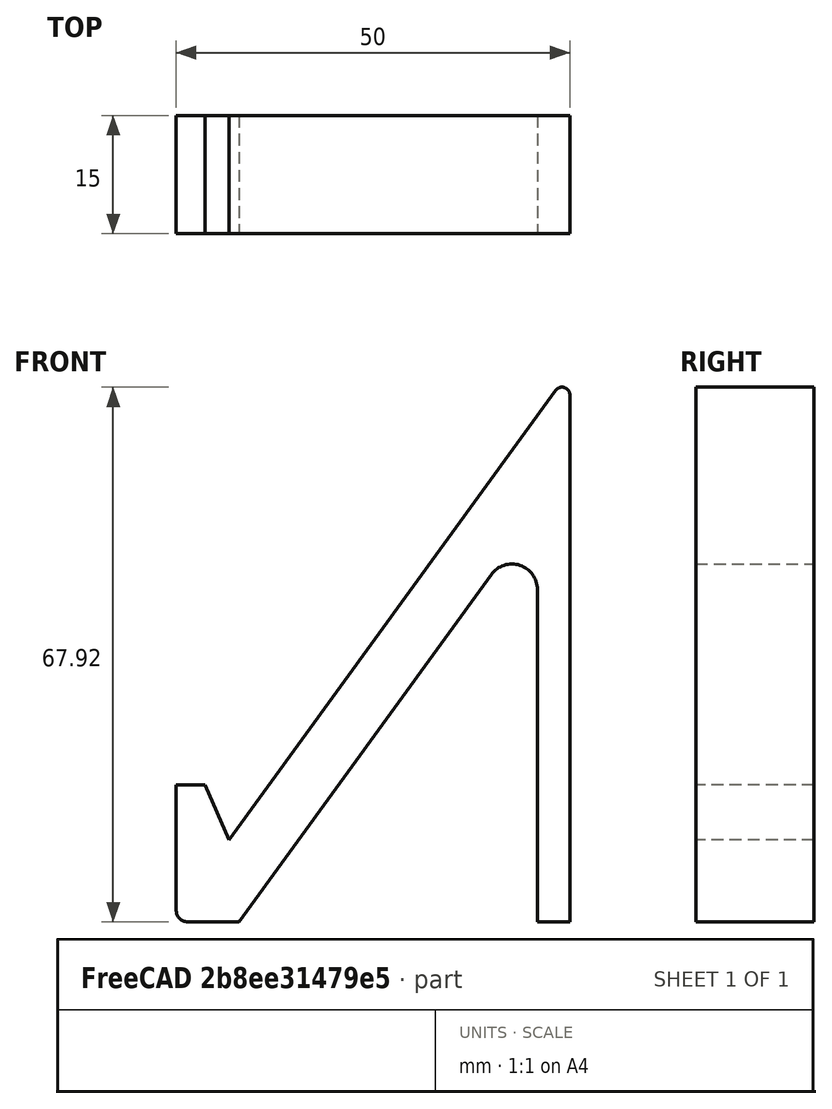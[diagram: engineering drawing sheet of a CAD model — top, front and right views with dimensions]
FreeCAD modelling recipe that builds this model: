
FCSTD DOCUMENT  (FreeCAD 1.1R20260414 (Git shallow))
Label: swordStand
License: All rights reserved
LicenseURL: https://en.wikipedia.org/wiki/All_rights_reserved
objects: App::Point×1, Sketcher::SketchObject×1, PartDesign::Pad×1, PartDesign::Fillet×1, PartDesign::Body×1
note: 9 computed .brp shape members not serialized (recipe doc carries the construction recipe); baked Part::Feature solids carry a one-line shape summary decoded from their .brp

FEATURE [App::Point] Origin001
  Role = Origin
FEATURE [Sketcher::SketchObject] Sketch
  ArcFitTolerance = 1e-06
  AttachmentSupport = -> [Origin]
  ExternalTypes = [0]
  FullyConstrained = false
  MakeInternals = false
  MapMode = 5
  Placement = pos=(0,0,0) rot=(1,0,0;1.5708rad)
  _ExternalGeoVersion = 1
  sketch-geometry (17):
    g0: LineSegment [constr] StartX=0 StartY=0 StartZ=0 EndX=50 EndY=0 EndZ=0
    g1: LineSegment [constr] StartX=50 StartY=0 StartZ=0 EndX=50 EndY=70 EndZ=0
    g2: LineSegment [constr] StartX=50 StartY=70 StartZ=0 EndX=0 EndY=70 EndZ=0
    g3: LineSegment [constr] StartX=0 StartY=70 StartZ=0 EndX=0 EndY=0 EndZ=0
    g4: LineSegment StartX=50 StartY=0 StartZ=0 EndX=49.9996 EndY=70.0003 EndZ=0
    g5: LineSegment StartX=49.9996 StartY=70.0003 StartZ=0 EndX=6.69318 EndY=10.4107 EndZ=0
    g6: LineSegment StartX=6.69318 StartY=10.4107 StartZ=0 EndX=3.65564 EndY=17.3888 EndZ=0
    g7: LineSegment StartX=3.65564 StartY=17.3888 StartZ=0 EndX=0 EndY=17.3888 EndZ=0
    g8: LineSegment StartX=0 StartY=17.3888 StartZ=0 EndX=0 EndY=1.42432 EndZ=0
    g9: LineSegment StartX=1.42432 StartY=0 StartZ=0 EndX=7.94682 EndY=0 EndZ=0
    g10: LineSegment StartX=7.94682 StartY=0 StartZ=0 EndX=40.0155 EndY=44.1265 EndZ=0
    g11: LineSegment StartX=45.8791 StartY=42.2209 StartZ=0 EndX=45.8791 EndY=0 EndZ=0
    g12: LineSegment StartX=45.8791 StartY=0 StartZ=0 EndX=50 EndY=0 EndZ=0
    g13: ArcOfCircle CenterX=42.6376 CenterY=42.2209 CenterZ=0 NormalX=0 NormalY=0 NormalZ=1 AngleXU=0 Radius=3.24142 StartAngle=-9e-16 EndAngle=2.51314
    g14: GeomPoint [constr] X=45.8791 Y=52.1947 Z=0
    g15: ArcOfCircle CenterX=1.42432 CenterY=1.42432 CenterZ=0 NormalX=0 NormalY=0 NormalZ=1 AngleXU=0 Radius=1.42432 StartAngle=3.14159 EndAngle=4.71239
    g16: GeomPoint [constr] X=0 Y=0 Z=0
  constraints (34):
    c: Coincident(g0,g1)
    c: Coincident(g1,g2)
    c: Coincident(g2,g3)
    c: Coincident(g3,g0)
    c: Horizontal(g2)
    c: Vertical(g1)
    c: Vertical(g3)
    c: Distance(g1,g3) = 50
    c: Distance(g0,g2) = 70
    c: Coincident(g0,g-1)
    c: Coincident(g0,g4)
    c: Coincident(g4,g5)
    c: Coincident(g5,g6)
    c: Coincident(g6,g7)
    c: PointOnObject(g7,g3)
    c: Horizontal(g7)
    c: Coincident(g7,g8)
    c: Coincident(g16,g0)
    c: PointOnObject(g9,g0)
    c: Horizontal(g9)
    c: Coincident(g9,g10)
    c: PointOnObject(g11,g0)
    c: Vertical(g11)
    c: Coincident(g11,g12)
    c: Coincident(g12,g0)
    c: PointOnObject(g14,g10)
    c: PointOnObject(g14,g11)
    c: Tangent(g10,g13) = 1.5708
    c: Tangent(g11,g13) = 1.5708
    c: PointOnObject(g16,g8)
    c: PointOnObject(g16,g9)
    c: Tangent(g8,g15) = -1.5708
    c: Tangent(g9,g15) = -1.5708
    c: Parallel(g10,g5)
FEATURE [PartDesign::Pad] Pad
  Direction = (0,-1,2e-16)
  Length = 15
  Length2 = 10
  Profile = -> Sketch
  ReferenceAxis = -> Sketch [N_Axis]
  Refine = true
  SideType = 0
  Suppressed = false
  Type = 0
  Type2 = 0
FEATURE [PartDesign::Fillet] Fillet
  Base = -> Pad [Edge8]
  BaseFeature = -> Pad
  Radius = 1
  Refine = true
  SupportTransform = false
  Suppressed = false
  UseAllEdges = false
FEATURE [PartDesign::Body] Body
  AllowCompound = true
  Group = -> [Sketch,Pad,Fillet]
  Origin = -> Origin
  Tip = -> Fillet
